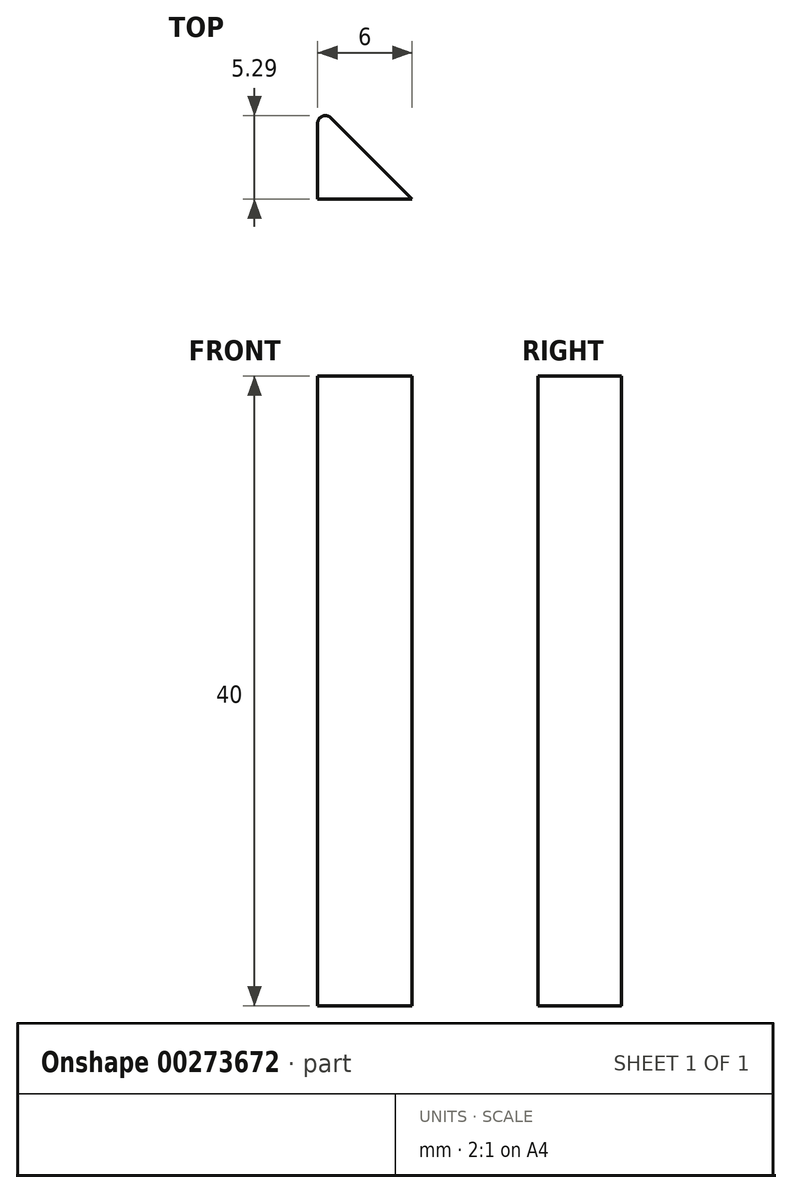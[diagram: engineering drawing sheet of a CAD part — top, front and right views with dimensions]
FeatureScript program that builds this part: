
annotation { "Feature Type Name" : "Feature", "Feature Type Description" : "" }
export const myFeature = defineFeature(function(context is Context, id is Id, definition is map)
    precondition{}
    {
        {
            var Q0;
            Q0=qCreatedBy(makeId("Top.planeOp"),FACE);
            var sketch = newSketch(context, id + "F0", { "sketchPlane" : qUnion([Q0])});
            skLineSegment(sketch, "E0.bottom", {"start": v(-61.58, 49.76) * mm, "end": v(-55.58, 49.76) * mm});
            skLineSegment(sketch, "E0.top", {"start": v(-61.58, 43.76) * mm, "end": v(-55.58, 43.76) * mm});
            skLineSegment(sketch, "E0.left", {"start": v(-61.58, 49.76) * mm, "end": v(-61.58, 43.76) * mm});
            skLineSegment(sketch, "E0.right", {"start": v(-55.58, 49.76) * mm, "end": v(-55.58, 43.76) * mm});
            skLineSegment(sketch, "E1", {"start": v(-61.58, 49.76) * mm, "end": v(-55.58, 43.76) * mm});
            skSolve(sketch);
        }
        {
            var Q0;
            Q0=makeQuery(id+"F0.imprint","IMPRINT",FACE,{"disambiguationData":[TD([[makeQuery(id+"F0.imprint","IMPRINT",EDGE,{"derivedFrom":sQuery(id+"F0.wireOp",EDGE,"E0.top")}),1.0]])]});
            extrude(context, id + "F1", {"entities" : qUnion([Q0]), "depth" : 40 * mm});
        }
        {
            var Q0;
            Q0=makeQuery(id+"F1.opExtrude","SWEPT_EDGE",EDGE,{"disambiguationData":[OSD([sQuery(id+"F0.wireOp",EDGE,"E0.bottom"),sQuery(id+"F0.wireOp",EDGE,"E0.left"),sQuery(id+"F0.wireOp",EDGE,"E1")])]});
            fillet(context, id + "F2", {"entities" : qUnion([Q0]), "radius" : 0.5 * mm, "tangentPropagation" : true, "allowEdgeOverflow" : false});
        }
    });
